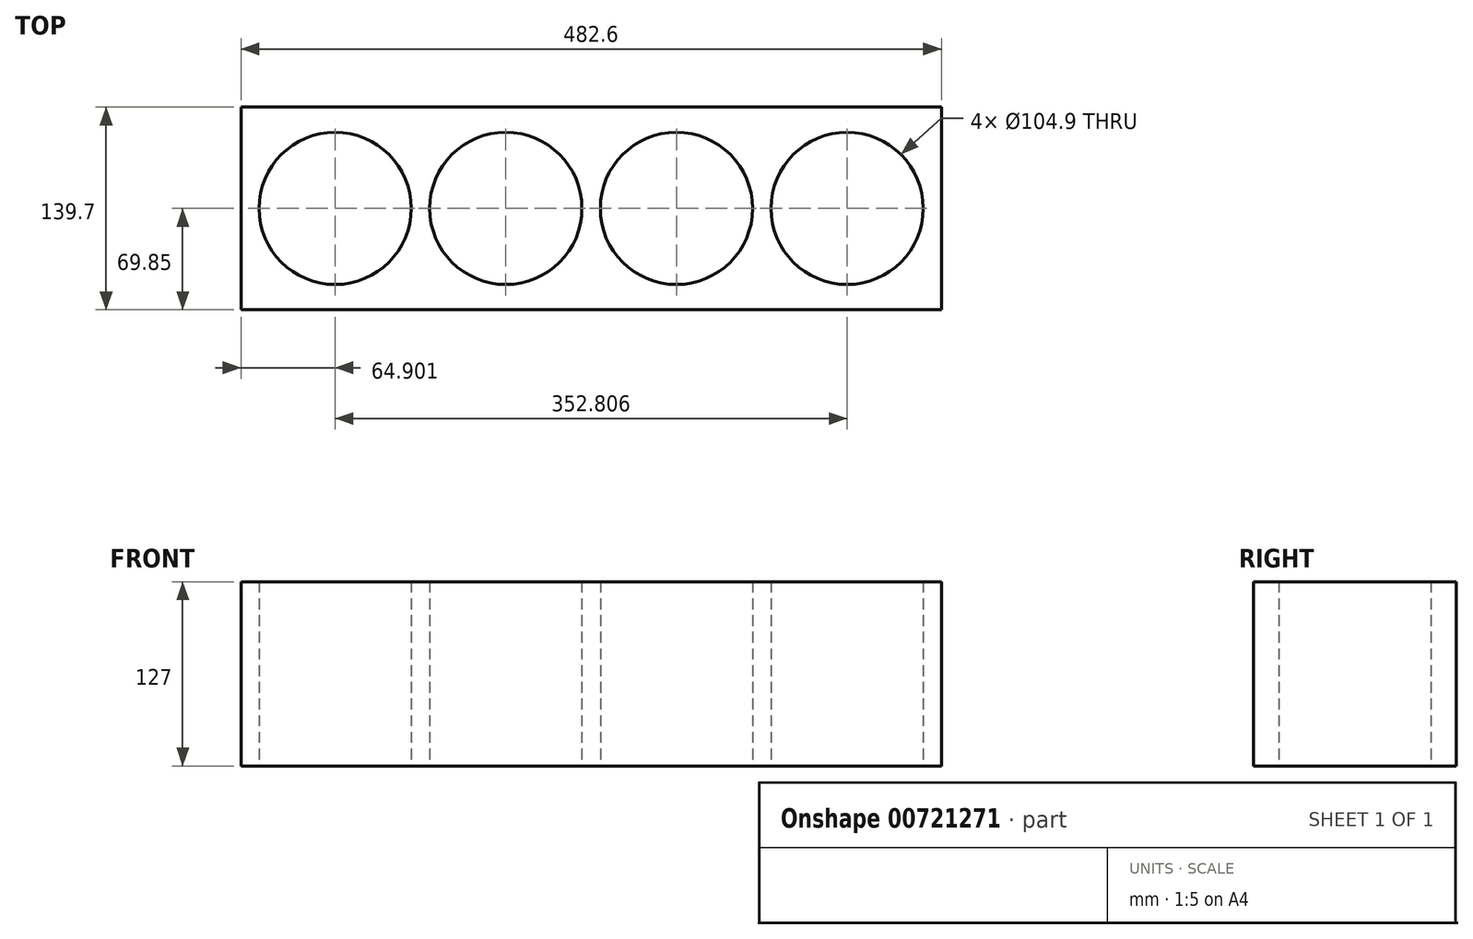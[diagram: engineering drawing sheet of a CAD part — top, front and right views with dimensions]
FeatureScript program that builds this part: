
annotation { "Feature Type Name" : "Feature", "Feature Type Description" : "" }
export const myFeature = defineFeature(function(context is Context, id is Id, definition is map)
    precondition{}
    {
        {
            var Q0;
            Q0=qCreatedBy(makeId("Top.planeOp"),FACE);
            var sketch = newSketch(context, id + "F0", { "sketchPlane" : qUnion([Q0])});
            skCircle(sketch, "E0", {"center": v(-163.1, 0) * mm, "radius": 52.45 * mm});
            skCircle(sketch, "E1.1.0.0", {"center": v(-45.5, 0) * mm, "radius": 52.45 * mm});
            skCircle(sketch, "E1.2.0.0", {"center": v(72.1, 0) * mm, "radius": 52.45 * mm});
            skCircle(sketch, "E1.3.0.0", {"center": v(189.7, 0) * mm, "radius": 52.45 * mm});
            skLineSegment(sketch, "E1.direction1", {"start": v(-163.1, 0) * mm, "end": v(-45.5, 0) * mm, "construction": true});
            skLineSegment(sketch, "E2", {"start": v(-163.1, 0) * mm, "end": v(189.7, 0) * mm, "construction": true});
            skLineSegment(sketch, "E3.bottom", {"start": v(254.6, -69.85) * mm, "end": v(-228, -69.85) * mm});
            skLineSegment(sketch, "E3.top", {"start": v(254.6, 69.85) * mm, "end": v(-228, 69.85) * mm});
            skLineSegment(sketch, "E3.left", {"start": v(254.6, -69.85) * mm, "end": v(254.6, 69.85) * mm});
            skLineSegment(sketch, "E3.right", {"start": v(-228, -69.85) * mm, "end": v(-228, 69.85) * mm});
            skPoint(sketch, "E3.middle", {"position": v(13.3, 0) * mm});
            skSolve(sketch);
        }
        {
            var Q0;
            Q0=makeQuery(id+"F0.imprint","IMPRINT",FACE,{"disambiguationData":[TD([[makeQuery(id+"F0.imprint","IMPRINT",EDGE,{"derivedFrom":sQuery(id+"F0.wireOp",EDGE,"E0")}),-1.0]])]});
            extrude(context, id + "F1", {"entities" : qUnion([Q0]), "depth" : 127 * mm, "offsetDistance" : 25.4 * mm});
        }
    });
